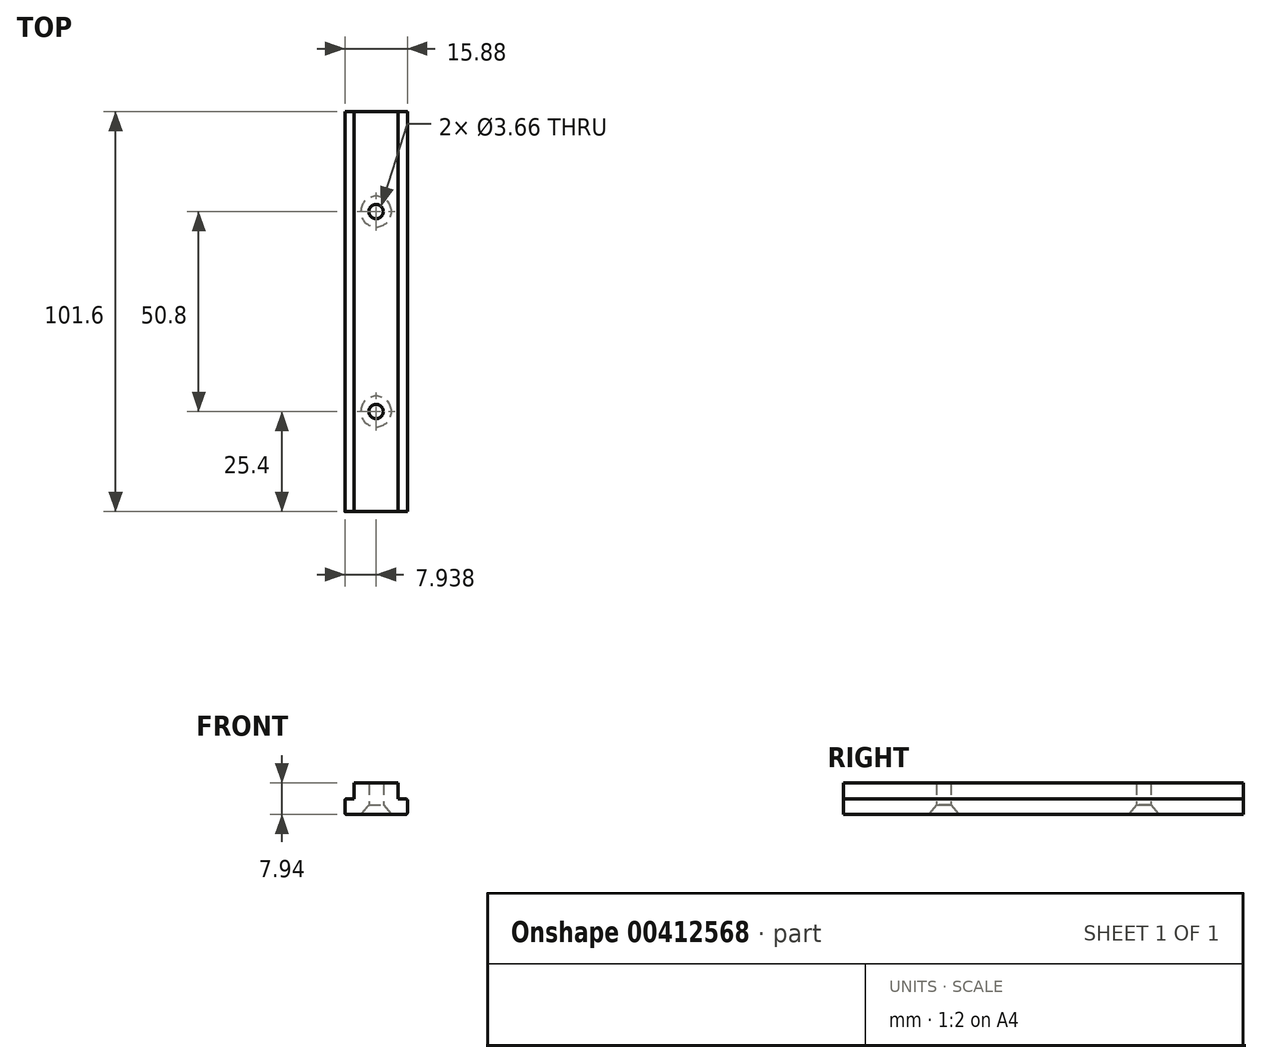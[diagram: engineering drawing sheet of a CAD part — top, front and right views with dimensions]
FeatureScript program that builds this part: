
annotation { "Feature Type Name" : "Feature", "Feature Type Description" : "" }
export const myFeature = defineFeature(function(context is Context, id is Id, definition is map)
    precondition{}
    {
        {
            var Q0;
            Q0=qCreatedBy(makeId("Front.planeOp"),FACE);
            var sketch = newSketch(context, id + "F0", { "sketchPlane" : qUnion([Q0])});
            skLineSegment(sketch, "E0.bottom", {"start": v(0, 0) * mm, "end": v(15.88, 0) * mm});
            skLineSegment(sketch, "E0.top", {"start": v(0, 3.97) * mm, "end": v(2.38, 3.97) * mm});
            skLineSegment(sketch, "E0.left", {"start": v(0, 0) * mm, "end": v(0, 3.97) * mm});
            skLineSegment(sketch, "E0.right", {"start": v(15.88, 0) * mm, "end": v(15.88, 3.97) * mm});
            skLineSegment(sketch, "E1.top", {"start": v(2.38, 7.94) * mm, "end": v(13.5, 7.94) * mm});
            skLineSegment(sketch, "E1.left", {"start": v(2.38, 3.97) * mm, "end": v(2.38, 7.94) * mm});
            skLineSegment(sketch, "E1.right", {"start": v(13.5, 3.97) * mm, "end": v(13.5, 7.94) * mm});
            skLineSegment(sketch, "E2.trimOffspring", {"start": v(13.5, 3.97) * mm, "end": v(15.88, 3.97) * mm});
            skLineSegment(sketch, "E3", {"start": v(7.94, 7.94) * mm, "end": v(7.94, 0) * mm, "construction": true});
            skSolve(sketch);
        }
        {
            var Q0;
            Q0=makeQuery(id+"F0.imprint","IMPRINT",FACE,{"disambiguationData":[TD([[makeQuery(id+"F0.imprint","IMPRINT",EDGE,{"derivedFrom":sQuery(id+"F0.wireOp",EDGE,"E0.bottom")}),1.0]])]});
            extrude(context, id + "F1", {"entities" : qUnion([Q0]), "depth" : 101.6 * mm});
        }
        {
            var Q0;
            Q0=makeQuery(id+"F1.opExtrude","SWEPT_FACE",FACE,{"disambiguationData":[OSD([sQuery(id+"F0.wireOp",EDGE,"E0.bottom")])]});
            var sketch = newSketch(context, id + "F2", { "sketchPlane" : qUnion([Q0])});
            skPoint(sketch, "E4", {"position": v(7.94, 76.2) * mm});
            skPoint(sketch, "E4.positionSnap0", {"position": v(7.94, 101.6) * mm});
            skPoint(sketch, "E5", {"position": v(7.94, 25.4) * mm});
            skPoint(sketch, "E5.positionSnap0", {"position": v(7.94, 0) * mm});
            skLineSegment(sketch, "E6", {"start": v(7.94, 101.6) * mm, "end": v(7.94, 76.2) * mm, "construction": true});
            skLineSegment(sketch, "E7", {"start": v(7.94, 25.4) * mm, "end": v(7.94, 0) * mm, "construction": true});
            skLineSegment(sketch, "E8", {"start": v(7.94, 25.4) * mm, "end": v(7.94, 50.8) * mm, "construction": true});
            skLineSegment(sketch, "E9", {"start": v(7.94, 50.8) * mm, "end": v(7.94, 76.2) * mm, "construction": true});
            skSolve(sketch);
        }
        {
            var Q0;
            Q0=makeQuery(id+"F1.opExtrude","SWEPT_EDGE",EDGE,{"disambiguationData":[OSD([sQuery(id+"F0.wireOp",EDGE,"E0.right"),sQuery(id+"F0.wireOp",EDGE,"E2.trimOffspring")])]});
            var Q1;
            Q1=makeQuery(id+"F1.opExtrude","SWEPT_EDGE",EDGE,{"disambiguationData":[OSD([sQuery(id+"F0.wireOp",EDGE,"E0.bottom"),sQuery(id+"F0.wireOp",EDGE,"E0.right")])]});
            var Q2;
            Q2=makeQuery(id+"F1.opExtrude","SWEPT_EDGE",EDGE,{"disambiguationData":[OSD([sQuery(id+"F0.wireOp",EDGE,"E0.top"),sQuery(id+"F0.wireOp",EDGE,"E0.left")])]});
            var Q3;
            Q3=makeQuery(id+"F1.opExtrude","SWEPT_EDGE",EDGE,{"disambiguationData":[OSD([sQuery(id+"F0.wireOp",EDGE,"E0.bottom"),sQuery(id+"F0.wireOp",EDGE,"E0.left")])]});
            fillet(context, id + "F3", {"entities" : qUnion([Q0, Q1, Q2, Q3]), "radius" : 0.4 * mm, "tangentPropagation" : true, "allowEdgeOverflow" : false});
        }
        {
            var Q0;
            Q0=sQuery(id+"F2.wireOp",VERTEX,"E4");
            var Q1;
            Q1=sQuery(id+"F2.wireOp",VERTEX,"E5");
            var Q2;
            Q2=makeQuery(id+"F1.opExtrude","SWEPT_BODY",BODY,{"disambiguationData":[OSD([sQuery(id+"F0.wireOp",EDGE,"E0.bottom"),sQuery(id+"F0.wireOp",EDGE,"E0.top"),sQuery(id+"F0.wireOp",EDGE,"E0.left"),sQuery(id+"F0.wireOp",EDGE,"E0.right"),sQuery(id+"F0.wireOp",EDGE,"E1.top"),sQuery(id+"F0.wireOp",EDGE,"E1.left"),sQuery(id+"F0.wireOp",EDGE,"E1.right"),sQuery(id+"F0.wireOp",EDGE,"E2.trimOffspring")])]});
            hole(context, id + "F4", {"style" : HoleStyle.C_SINK, "endStyle" : HoleEndStyle.THROUGH, "standardTappedOrClearance" : lookupTablePath({ "standard" : "ANSI", "fit" : "Close", "size" : "#6", "type" : "Clearance" }), "standardBlindInLast" : lookupTablePath({ "fit" : "Close", "standard" : "ANSI", "size" : "#6", "type" : "Clearance" }), "holeDiameter" : 3.66 * mm, "cSinkDiameter" : 7.8 * mm, "cSinkAngle" : 82 * degree, "isTappedThrough" : true, "tappedDepth" : 12.7 * mm, "tapClearance" : 3, "startFromSketch" : true, "locations" : qUnion([Q0, Q1]), "scope" : qUnion([Q2])});
        }
    });
